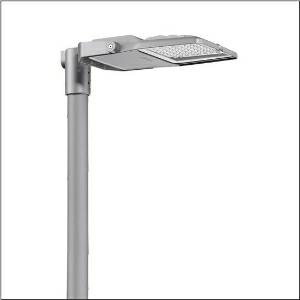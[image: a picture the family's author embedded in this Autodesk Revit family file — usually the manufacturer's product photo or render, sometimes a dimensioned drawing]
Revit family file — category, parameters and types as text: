
# Revit family: floodlight_fl_21_mini___pl33t_5xa7776d2f3a_276e
name_source: partatom
category: Lighting Fixtures
units: mm (PartAtom-declared; Revit-internal decimal feet)

## family parameters
Cut with Voids When Loaded = No
Host = Face
Light Source = No
Part Type = Normal
Room Calculation Point = No
Round Connector Dimension = Use Diameter
Shared = No

## types (1)
- --- (1 x LED, 17630 lm, 142.9 W, 3000K)
    Apparent Load = 143 VA
    CIE Flux Codes = 26 75 99 100 100
    Color Rendering = 70
    Color Temperature = 3000K
    Default Elevation = 1800 mm
    Description = Floodlight FL 21 mini, floodlight, primary light control with lens, of PMMA, primary optical cover: protective disc, of toughened safety glass, transparent, light distribution: PL33T, light emission: direct distribution, installation type: surface-mounted, LED, High Power LED, rated luminous flux: 17.630lm, luminous efficacy: 123lm/W, light colour: 730, colour temperature: 3000K, control gear: Smart Interface (Zhaga), control: flexible luminous flux parameterisation, time-dependent luminous flux control, constant luminous flux control, overheat protection, pre-setting: logarithmic dimming characteristic, with terminal, 6-pole, mains connection: 220..240V, AC, 50/60Hz, start of lifetime: 143W, end of service life: 151W, reduction: 63W, luminaire housing, of diecast aluminium, powder-coated, SITECO metallic grey (DB 702S), corrosivity category C5 mid according to DIN EN ISO 12944, suitable for swimming pools, chlorine-resistant, sealing non-destructively replaceable, please order mast flange separately, mast bracket, of steel, galvanised, powder-coated, SITECO metallic grey (DB 702S), Smart Interface below and above, protection rating (complete): IP66, insulation class (complete): insulation class II (safety insulation), certification: CE, ENEC, VDE, protection symbol: D, impact resistance: IK08, permissible operating ambient temperature: -40..+40°C, permissible operating ambient temperature for outdoor applications: -40..+50°C, standard: DIN EN 12944, LABS conformity tested according to VDMA 24364:2018-05, packaging unit: 1 piece

Light Distribution: PL33T
    Height = 70 mm
    Lamp = 1 x LED
    Lamp Light Flux = 17630 lm
    Lamp Power = 142.9 W
    Lamp count = 1
    Length = 485 mm
    Luminous efficacy = 123 lm/W
    Manufacturer = Siteco
    ModVariant = No
    Model = 5XA7776D2F3A
    Number of Poles = 1
    OnlyDefault = Yes
    Power Factor = 1
    Product Name = Floodlight FL 21 mini | PL33T
    Product group = floodlight | pylon annexe
    ProductGroupID = 6201
    Protection Class = Protection class II
    Protection Degree = IP 66
    RLX_Detail_Level = 1
    RLX_Emergency_Light_Flux = 0 lm
    RLX_Emergency_Type = 0
    RLX_Emergency_Type_DB = No
    RlxData = <blob elided: 101193 chars, md5=5fe8995e>
    Socket = socket
    Standby Power = 0 W
    System Light Flux = 17630 lm
    System Power = 143 W
    Type Comments = factory setting: luminous flux: 100 % | dim-lin: 254 | 730 mA
    Type Image = l_1007125.jpg
    URL = http://relux.com
    VarID = @adj_147821
    Voltage = 0 V
    Weight = 0.00 kg
    Width = 337 mm

## geometry (parser evidence)
native form markers: Blend x4, Sweep x10
no freeform markers — native parametric forms only
